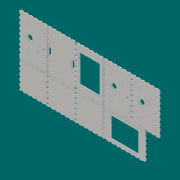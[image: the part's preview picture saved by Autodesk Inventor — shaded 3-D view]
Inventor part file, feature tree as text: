
AUTODESK INVENTOR PART (.ipt)
format: ipt  version: 2016 SP2 (Build 200236200, 236)  size: 1,688,064 bytes
history: native  units: in
note: dims shown in document units (in); Inventor stores cm internally (conversion verified against a paired STEP export)
features: reference x12, extrude x2, sketch x2, other x1, plane x1
ambient origin geometry x8: Origin, YZ Plane, XZ Plane, XY Plane, X Axis, Y Axis, Z Axis, Center Point
bodies: Solid1 (feature_tree)
feature tree (18):
  other  "<userpath>\oneDrive\projects\splitFlapDisplay\parameters.xlsx"
  extrude  "Extrusion1"  Depth=0.0047in
  plane  "Work Plane2"
  extrude  "Extrusion3"  Depth=0.0047in
  sketch  "Sketch1"  dims[d0=0.0047in d1=0.0047in]
  reference  "Reference1"
  reference  "Reference2"
  reference  "Reference3"
  reference  "Reference4"
  reference  "Reference5"
  reference  "Reference6"
  reference  "Reference7"
  reference  "Reference8"
  reference  "Reference9"
  reference  "Reference10"
  reference  "Reference11"
  sketch  "Sketch3"  dims[d2=0.0047in d3=0.0047in d4=0.0047in d5=0.0047in d6=0.0047in d7=0.0047in d8=0.0047in d9=0.0047in d10=0.0047in d11=0.0047in d12=0.0047in d13=0.0047in d14=0.0047in d15=0.0047in d16=0.0047in d17=0.0047in d18=0.0047in d19=0.0047in d20=0.0047in d21=0.0047in d22=0.0047in d23=0.0047in d24=0.0047in d25=0.0047in d26=0.0047in d27=0.0047in d28=0.0047in d29=0.0047in d30=0.0047in d31=0.0047in d32=0.0047in d33=0.0047in d34=0.0047in d35=0.0047in d36=0.0047in d37=0.0047in d38=0.0047in d39=0.125in d40=0.0in d54=0.0047in d55=0.0047in d56=0.0047in d57=0.0047in d58=0.0047in d59=0.0047in d60=0.0047in d61=0.0047in d62=0.0047in d63=0.0047in d64=0.0047in d65=0.125in d66=0.0in]
  reference  "Reference13"
